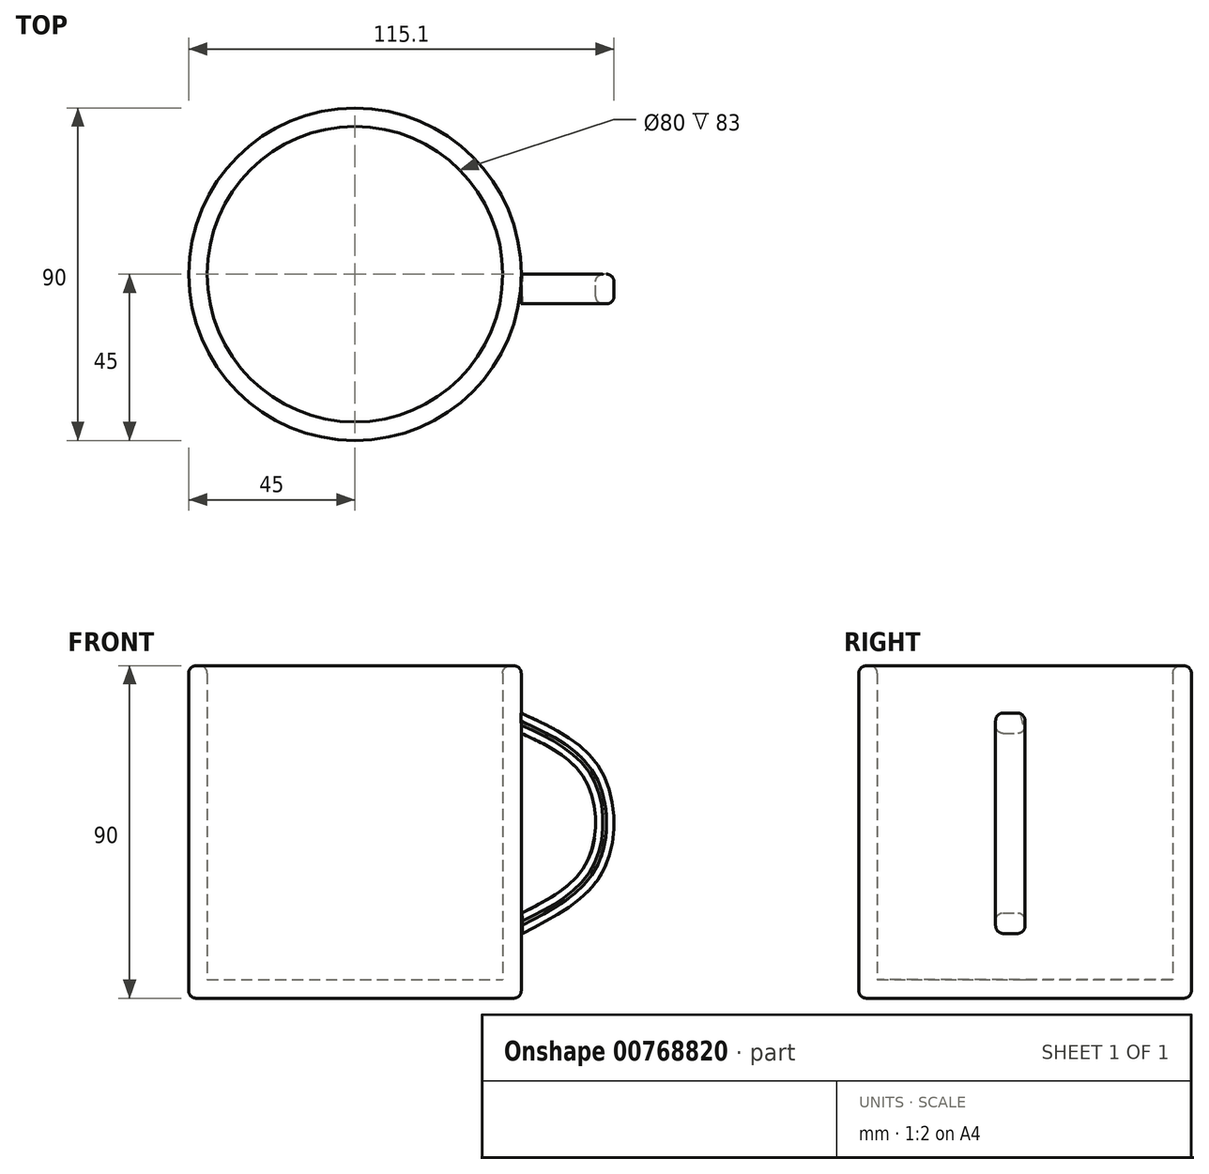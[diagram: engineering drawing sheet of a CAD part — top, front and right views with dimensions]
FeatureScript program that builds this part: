
annotation { "Feature Type Name" : "Feature", "Feature Type Description" : "" }
export const myFeature = defineFeature(function(context is Context, id is Id, definition is map)
    precondition{}
    {
        {
            var Q0;
            Q0=qCreatedBy(makeId("Front.planeOp"),FACE);
            var sketch = newSketch(context, id + "F0", { "sketchPlane" : qUnion([Q0])});
            skLineSegment(sketch, "E0", {"start": v(0, -44.4) * mm, "end": v(40, -44.4) * mm});
            skLineSegment(sketch, "E1", {"start": v(40, -44.4) * mm, "end": v(40, 40.6) * mm});
            skLineSegment(sketch, "E2", {"start": v(40, 40.6) * mm, "end": v(45, 40.6) * mm});
            skLineSegment(sketch, "E3", {"start": v(45, 40.6) * mm, "end": v(45, -49.4) * mm});
            skLineSegment(sketch, "E4", {"start": v(0, -49.4) * mm, "end": v(0, -44.4) * mm});
            skLineSegment(sketch, "E5", {"start": v(0, -49.4) * mm, "end": v(45, -49.4) * mm});
            skSolve(sketch);
        }
        {
            var Q0;
            Q0=makeQuery(id+"F0.imprint","IMPRINT",FACE,{"disambiguationData":[TD([[makeQuery(id+"F0.imprint","IMPRINT",EDGE,{"derivedFrom":sQuery(id+"F0.wireOp",EDGE,"E0")}),-1.0]])]});
            var Q1;
            Q1=sQuery(id+"F0.wireOp",EDGE,"E4");
            revolve(context, id + "F1", {"surfaceOperationType" : NewSurfaceOperationType.NEW, "entities" : qUnion([Q0]), "axis" : qUnion([Q1]), "revolveType" : RevolveType.FULL});
        }
        {
            var Q0;
            Q0=makeQuery(id+"F1.opRevolve","SWEPT_EDGE",EDGE,{"disambiguationData":[OSD([sQuery(id+"F0.wireOp",EDGE,"E3"),sQuery(id+"F0.wireOp",EDGE,"E5")])]});
            fillet(context, id + "F2", {"entities" : qUnion([Q0]), "radius" : 2 * mm, "tangentPropagation" : true, "allowEdgeOverflow" : false});
        }
        {
            var Q0;
            Q0=makeQuery(id+"F1.opRevolve","SWEPT_EDGE",EDGE,{"disambiguationData":[OSD([sQuery(id+"F0.wireOp",EDGE,"E2"),sQuery(id+"F0.wireOp",EDGE,"E3")])]});
            fillet(context, id + "F3", {"entities" : qUnion([Q0]), "radius" : 2 * mm, "tangentPropagation" : true, "allowEdgeOverflow" : false});
        }
        {
            var Q0;
            Q0=makeQuery(id+"F1.opRevolve","SWEPT_EDGE",EDGE,{"disambiguationData":[OSD([sQuery(id+"F0.wireOp",EDGE,"E1"),sQuery(id+"F0.wireOp",EDGE,"E2")])]});
            fillet(context, id + "F4", {"entities" : qUnion([Q0]), "radius" : 2 * mm, "tangentPropagation" : true, "allowEdgeOverflow" : false});
        }
        {
            var Q0;
            Q0=qCreatedBy(makeId("Front.planeOp"),FACE);
            var sketch = newSketch(context, id + "F5", { "sketchPlane" : qUnion([Q0])});
            skFitSpline(sketch, "E6", {"points": [v(44.98, 27.8) * mm, v(66.52, 12.37) * mm, v(67.1, -15) * mm, v(45.27, -31.88) * mm], "startDerivative": vector(77.88, -35.54) * mm, "endDerivative": vector(-78.52, -39.47) * mm});
            skFitSpline(sketch, "E7.0", {"points": [v(42.9, 23.25) * mm, v(44.53, 22.51) * mm, v(47.71, 21.06) * mm, v(52.14, 18.82) * mm, v(55.4, 16.81) * mm, v(57.67, 15.09) * mm, v(59.2, 13.73) * mm, v(60.53, 12.29) * mm, v(61.69, 10.75) * mm, v(62.66, 9.1) * mm, v(63.5, 7.22) * mm, v(64.18, 5.18) * mm, v(64.69, 3) * mm, v(65, 0.73) * mm, v(65.13, -1.58) * mm, v(65.07, -3.89) * mm, v(64.8, -6.15) * mm, v(64.36, -8.33) * mm, v(63.73, -10.38) * mm, v(63.06, -11.95) * mm, v(62.46, -13.1) * mm, v(61.78, -14.2) * mm, v(60.83, -15.53) * mm, v(59.04, -17.54) * mm, v(56.31, -19.89) * mm, v(52.36, -22.5) * mm, v(47.88, -24.97) * mm, v(44.66, -26.59) * mm, v(43.03, -27.41) * mm]});
            skLineSegment(sketch, "E8", {"start": v(44.98, 27.8) * mm, "end": v(45, 22.3) * mm});
            skLineSegment(sketch, "E9.trimOffspring", {"start": v(45.24, -26.3) * mm, "end": v(45.27, -31.88) * mm});
            skSolve(sketch);
        }
        {
            var Q0;
            Q0=makeQuery(id+"F5.imprint","IMPRINT",FACE,{"disambiguationData":[TD([[makeQuery(id+"F5.imprint","IMPRINT",EDGE,{"derivedFrom":sQuery(id+"F5.wireOp",EDGE,"E6")}),-1.0]])]});
            extrude(context, id + "F6", {"entities" : qUnion([Q0]), "operationType" : NewBodyOperationType.ADD, "depth" : 8 * mm, "offsetDistance" : 25 * mm});
        }
        {
            var Q0;
            Q0=makeQuery(id+"F6.opExtrude","CAP_EDGE",EDGE,{"disambiguationData":[OSD([sQuery(id+"F5.wireOp",EDGE,"E6")])],"isStart":false});
            var Q1;
            Q1=makeQuery(id+"F6.opExtrude","CAP_EDGE",EDGE,{"disambiguationData":[OSD([sQuery(id+"F5.wireOp",EDGE,"E6")])],"isStart":true});
            var Q2;
            Q2=makeQuery(id+"F6.opExtrude","CAP_EDGE",EDGE,{"disambiguationData":[OSD([sQuery(id+"F5.wireOp",EDGE,"E7.0")])],"isStart":false});
            fillet(context, id + "F7", {"entities" : qUnion([Q0, Q1, Q2]), "radius" : 2 * mm, "tangentPropagation" : true, "allowEdgeOverflow" : false});
        }
        {
            var Q0;
            Q0=makeQuery(id+"F6.opExtrude","CAP_EDGE",EDGE,{"disambiguationData":[OSD([sQuery(id+"F5.wireOp",EDGE,"E7.0")])],"isStart":true});
            fillet(context, id + "F8", {"entities" : qUnion([Q0]), "radius" : 2 * mm, "tangentPropagation" : true, "allowEdgeOverflow" : false});
        }
    });
